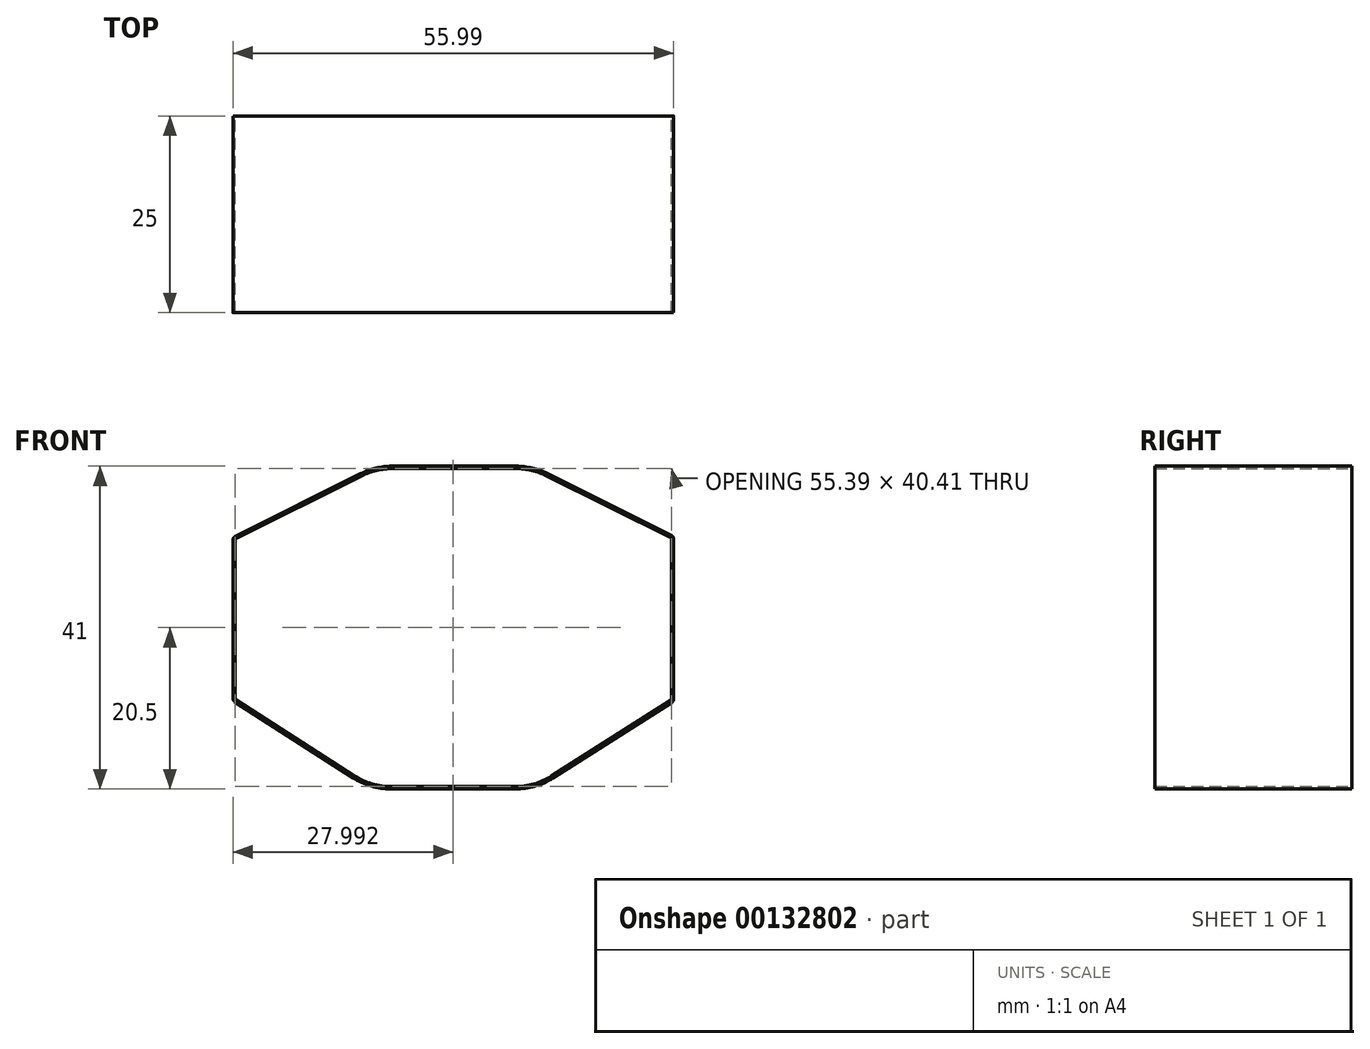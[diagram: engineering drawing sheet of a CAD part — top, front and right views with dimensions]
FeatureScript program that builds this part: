
annotation { "Feature Type Name" : "Feature", "Feature Type Description" : "" }
export const myFeature = defineFeature(function(context is Context, id is Id, definition is map)
    precondition{}
    {
        {
            var Q0;
            Q0=qCreatedBy(makeId("Front.planeOp"),FACE);
            var sketch = newSketch(context, id + "F0", { "sketchPlane" : qUnion([Q0])});
            skLineSegment(sketch, "E0", {"start": v(-7.9, 1.56) * mm, "end": v(7.82, 1.56) * mm});
            skLineSegment(sketch, "E1", {"start": v(12.65, 2.96) * mm, "end": v(27.74, 12.56) * mm});
            skLineSegment(sketch, "E2", {"start": v(27.98, 12.98) * mm, "end": v(27.98, 33.32) * mm});
            skLineSegment(sketch, "E3", {"start": v(27.7, 33.76) * mm, "end": v(11.96, 41.62) * mm});
            skLineSegment(sketch, "E4", {"start": v(7.94, 42.56) * mm, "end": v(-7.76, 42.56) * mm});
            skLineSegment(sketch, "E5", {"start": v(-11.79, 41.61) * mm, "end": v(-27.74, 33.63) * mm});
            skLineSegment(sketch, "E6", {"start": v(-28.01, 33.18) * mm, "end": v(-28.01, 13.06) * mm});
            skLineSegment(sketch, "E7", {"start": v(-27.78, 12.64) * mm, "end": v(-12.78, 2.99) * mm});
            skPoint(sketch, "E8.visualSharp", {"position": v(-9.89, 42.56) * mm});
            skArc(sketch, "E8.filletArc", {"start": v(-7.76, 42.56) * mm, "mid": v(-9.83, 42.32) * mm, "end": v(-11.79, 41.61) * mm});
            skPoint(sketch, "E9.visualSharp", {"position": v(10.06, 42.56) * mm});
            skArc(sketch, "E9.filletArc", {"start": v(11.96, 41.62) * mm, "mid": v(10, 42.32) * mm, "end": v(7.94, 42.56) * mm});
            skPoint(sketch, "E10.visualSharp", {"position": v(10.44, 1.56) * mm});
            skArc(sketch, "E10.filletArc", {"start": v(7.82, 1.56) * mm, "mid": v(10.33, 1.91) * mm, "end": v(12.65, 2.96) * mm});
            skPoint(sketch, "E11.visualSharp", {"position": v(-10.55, 1.56) * mm});
            skArc(sketch, "E11.filletArc", {"start": v(-12.78, 2.99) * mm, "mid": v(-10.44, 1.92) * mm, "end": v(-7.9, 1.56) * mm});
            skPoint(sketch, "E12.visualSharp", {"position": v(-28.01, 33.49) * mm});
            skArc(sketch, "E12.filletArc", {"start": v(-27.74, 33.63) * mm, "mid": v(-27.94, 33.44) * mm, "end": v(-28.01, 33.18) * mm});
            skPoint(sketch, "E13.visualSharp", {"position": v(27.98, 33.63) * mm});
            skArc(sketch, "E13.filletArc", {"start": v(27.98, 33.32) * mm, "mid": v(27.9, 33.58) * mm, "end": v(27.7, 33.76) * mm});
            skPoint(sketch, "E14.visualSharp", {"position": v(27.98, 12.71) * mm});
            skArc(sketch, "E14.filletArc", {"start": v(27.74, 12.56) * mm, "mid": v(27.91, 12.74) * mm, "end": v(27.98, 12.98) * mm});
            skPoint(sketch, "E15.visualSharp", {"position": v(-28.01, 12.79) * mm});
            skArc(sketch, "E15.filletArc", {"start": v(-28.01, 13.06) * mm, "mid": v(-27.95, 12.82) * mm, "end": v(-27.78, 12.64) * mm});
            skLineSegment(sketch, "E16.0", {"start": v(-27.62, 12.9) * mm, "end": v(-12.61, 3.24) * mm});
            skArc(sketch, "E16.1", {"start": v(-27.71, 13.06) * mm, "mid": v(-27.69, 12.96) * mm, "end": v(-27.62, 12.9) * mm});
            skLineSegment(sketch, "E16.2", {"start": v(-27.71, 33.18) * mm, "end": v(-27.71, 13.06) * mm});
            skArc(sketch, "E16.3", {"start": v(-27.6, 33.36) * mm, "mid": v(-27.68, 33.29) * mm, "end": v(-27.71, 33.18) * mm});
            skLineSegment(sketch, "E16.4", {"start": v(-11.65, 41.34) * mm, "end": v(-27.6, 33.36) * mm});
            skArc(sketch, "E16.5", {"start": v(27.58, 12.82) * mm, "mid": v(27.65, 12.89) * mm, "end": v(27.68, 12.98) * mm});
            skLineSegment(sketch, "E16.6", {"start": v(12.49, 3.21) * mm, "end": v(27.58, 12.82) * mm});
            skArc(sketch, "E16.7", {"start": v(7.82, 1.86) * mm, "mid": v(10.25, 2.2) * mm, "end": v(12.49, 3.21) * mm});
            skLineSegment(sketch, "E16.8", {"start": v(-7.9, 1.86) * mm, "end": v(7.82, 1.86) * mm});
            skLineSegment(sketch, "E16.9", {"start": v(27.68, 12.98) * mm, "end": v(27.68, 33.32) * mm});
            skArc(sketch, "E16.10", {"start": v(27.68, 33.32) * mm, "mid": v(27.65, 33.42) * mm, "end": v(27.57, 33.5) * mm});
            skLineSegment(sketch, "E16.11", {"start": v(27.57, 33.5) * mm, "end": v(11.83, 41.35) * mm});
            skArc(sketch, "E16.12", {"start": v(11.83, 41.35) * mm, "mid": v(9.94, 42.03) * mm, "end": v(7.94, 42.26) * mm});
            skLineSegment(sketch, "E16.13", {"start": v(7.94, 42.26) * mm, "end": v(-7.76, 42.26) * mm});
            skArc(sketch, "E16.14", {"start": v(-12.61, 3.24) * mm, "mid": v(-10.36, 2.2) * mm, "end": v(-7.9, 1.86) * mm});
            skArc(sketch, "E16.15", {"start": v(-7.76, 42.26) * mm, "mid": v(-9.76, 42.03) * mm, "end": v(-11.65, 41.34) * mm});
            skSolve(sketch);
        }
        {
            var Q0;
            Q0=makeQuery(id+"F0.imprint","IMPRINT",FACE,{"disambiguationData":[TD([[makeQuery(id+"F0.imprint","IMPRINT",EDGE,{"derivedFrom":sQuery(id+"F0.wireOp",EDGE,"E0")}),1.0]])]});
            extrude(context, id + "F1", {"entities" : qUnion([Q0]), "endBound" : BoundingType.SYMMETRIC, "depth" : 25 * mm});
        }
    });
